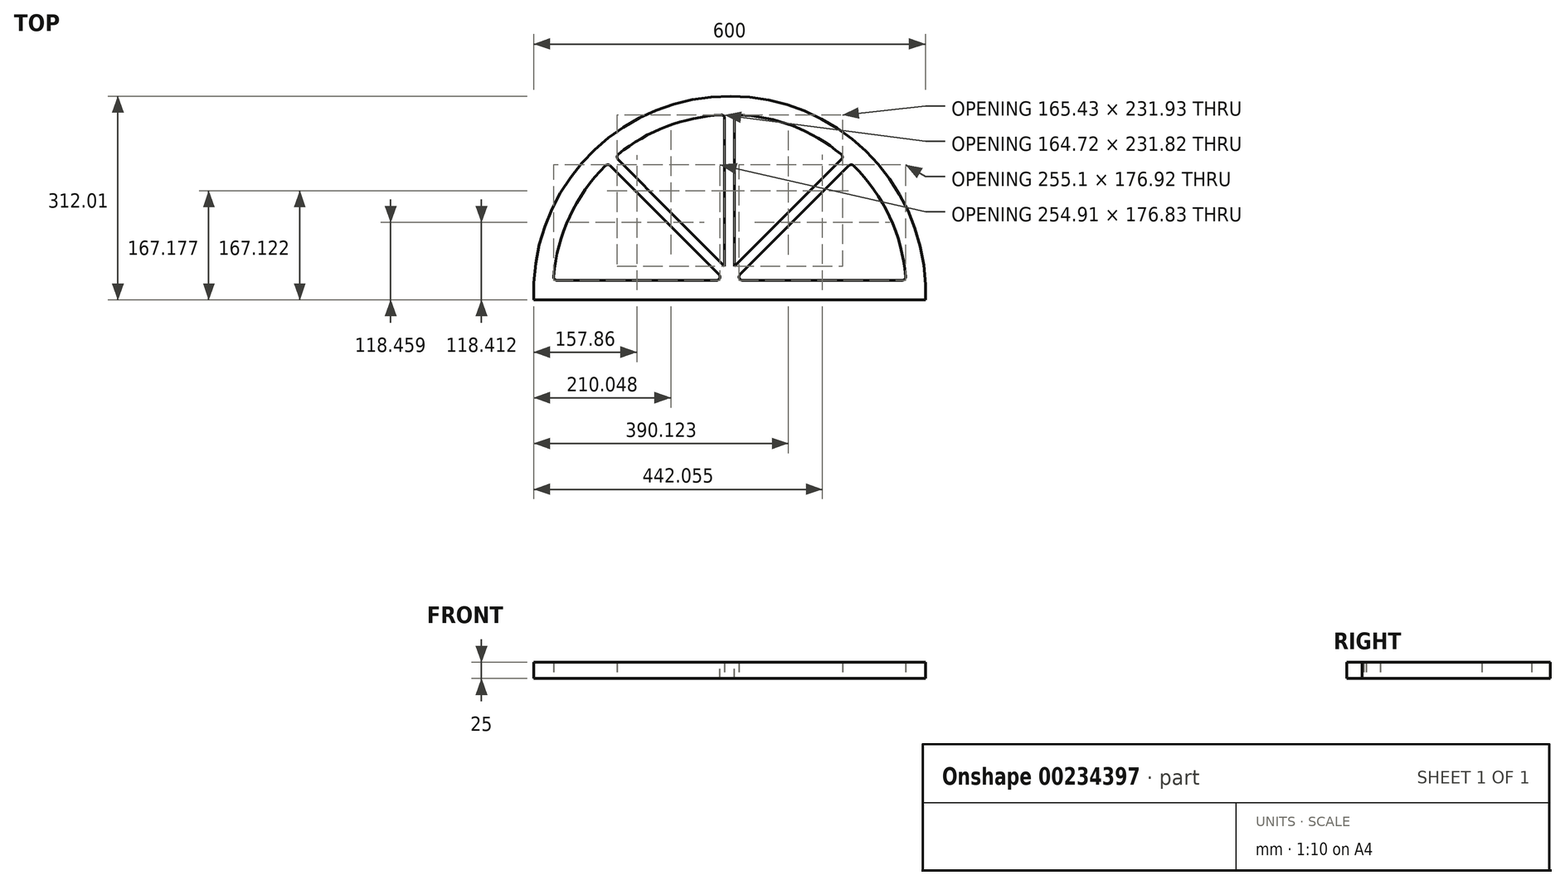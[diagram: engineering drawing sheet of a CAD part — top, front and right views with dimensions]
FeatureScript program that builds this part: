
annotation { "Feature Type Name" : "Feature", "Feature Type Description" : "" }
export const myFeature = defineFeature(function(context is Context, id is Id, definition is map)
    precondition{}
    {
        {
            var Q0;
            Q0=qCreatedBy(makeId("Top.planeOp"),FACE);
            var sketch = newSketch(context, id + "F0", { "sketchPlane" : qUnion([Q0])});
            skLineSegment(sketch, "E0", {"start": v(-299.9, -42.43) * mm, "end": v(300.1, -42.43) * mm});
            skLineSegment(sketch, "E1", {"start": v(-299.9, -42.43) * mm, "end": v(-299.9, -12.43) * mm});
            skLineSegment(sketch, "E2", {"start": v(300.1, -42.43) * mm, "end": v(300.1, -12.43) * mm});
            skArc(sketch, "E3", {"start": v(300.1, -42.43) * mm, "mid": v(-1.39, 269.57) * mm, "end": v(-299.9, -45.27) * mm});
            skLineSegment(sketch, "E4", {"start": v(-299.9, -12.43) * mm, "end": v(-299.7, -12.43) * mm});
            skLineSegment(sketch, "E5", {"start": v(300.1, -12.43) * mm, "end": v(299.77, -12.43) * mm});
            skArc(sketch, "E6", {"start": v(270.1, -12.43) * mm, "mid": v(245.18, 84.94) * mm, "end": v(186.44, 166.5) * mm});
            skPoint(sketch, "E7.start.orphan", {"position": v(0, -42.43) * mm});
            skLineSegment(sketch, "E8", {"start": v(-7.5, 49.69) * mm, "end": v(-7.5, 8.78) * mm});
            skLineSegment(sketch, "E9", {"start": v(-7.5, 49.69) * mm, "end": v(-7.5, 240.8) * mm});
            skLineSegment(sketch, "E10", {"start": v(7.5, 49.69) * mm, "end": v(7.5, 8.78) * mm});
            skPoint(sketch, "E11", {"position": v(-7.5, 240.8) * mm});
            skPoint(sketch, "E12", {"position": v(7.5, 240.8) * mm});
            skLineSegment(sketch, "E13", {"start": v(-269.9, -12.43) * mm, "end": v(-7.5, -12.43) * mm});
            skLineSegment(sketch, "E14", {"start": v(7.5, -12.43) * mm, "end": v(270.1, -12.43) * mm});
            skPoint(sketch, "E15.orphan", {"position": v(-7.5, -42.43) * mm});
            skPoint(sketch, "E16.orphan", {"position": v(7.5, -42.43) * mm});
            skPoint(sketch, "E17", {"position": v(0, -12.47) * mm});
            skLineSegment(sketch, "E18", {"start": v(-7.5, -12.43) * mm, "end": v(-186.35, 166.41) * mm});
            skLineSegment(sketch, "E19", {"start": v(-86.32, 87.6) * mm, "end": v(-174.62, 176.93) * mm});
            skLineSegment(sketch, "E20", {"start": v(-86.32, 87.6) * mm, "end": v(-7.5, 8.78) * mm});
            skPoint(sketch, "E21.start.orphan", {"position": v(-96.92, 76.99) * mm});
            skArc(sketch, "E22.trimOffspring", {"start": v(-186.35, 166.41) * mm, "mid": v(-245.02, 84.88) * mm, "end": v(-269.9, -12.43) * mm});
            skLineSegment(sketch, "E23", {"start": v(7.5, -12.43) * mm, "end": v(186.44, 166.5) * mm});
            skLineSegment(sketch, "E24", {"start": v(86.36, 87.64) * mm, "end": v(7.5, 8.78) * mm});
            skLineSegment(sketch, "E25", {"start": v(86.36, 87.64) * mm, "end": v(175.26, 176.54) * mm});
            skPoint(sketch, "E26.start.orphan", {"position": v(96.97, 77.04) * mm});
            skArc(sketch, "E27.trimOffspring", {"start": v(-7.5, 240.8) * mm, "mid": v(-96.5, 223.08) * mm, "end": v(-174.62, 176.93) * mm});
            skLineSegment(sketch, "E28", {"start": v(7.5, 49.69) * mm, "end": v(7.5, 240.8) * mm});
            skArc(sketch, "E29", {"start": v(175.26, 176.54) * mm, "mid": v(97.2, 223.87) * mm, "end": v(7.5, 240.8) * mm});
            skSolve(sketch);
        }
        {
            var Q0;
            {var subQ2=sQuery(id+"F0.wireOp",EDGE,"E0");Q0=makeQuery(id+"F0.imprint","IMPRINT",FACE,{"disambiguationData":[TD([[makeQuery(id+"F0.imprint","IMPRINT",EDGE,{"derivedFrom":subQ2}),1.0]])]});}
            extrude(context, id + "F1", {"entities" : qUnion([Q0]), "depth" : 25 * mm});
        }
        {
            var Q0;
            Q0=makeQuery(id+"F1.opExtrude","SWEPT_EDGE",EDGE,{"disambiguationData":[OSD([sQuery(id+"F0.wireOp",EDGE,"E9"),sQuery(id+"F0.wireOp",EDGE,"E27.trimOffspring")])]});
            var Q1;
            Q1=makeQuery(id+"F1.opExtrude","SWEPT_EDGE",EDGE,{"disambiguationData":[OSD([sQuery(id+"F0.wireOp",EDGE,"E25"),sQuery(id+"F0.wireOp",EDGE,"E29")])]});
            var Q2;
            Q2=makeQuery(id+"F1.opExtrude","SWEPT_EDGE",EDGE,{"disambiguationData":[OSD([sQuery(id+"F0.wireOp",EDGE,"E6"),sQuery(id+"F0.wireOp",EDGE,"E14")])]});
            var Q3;
            Q3=makeQuery(id+"F1.opExtrude","SWEPT_EDGE",EDGE,{"disambiguationData":[OSD([sQuery(id+"F0.wireOp",EDGE,"E28"),sQuery(id+"F0.wireOp",EDGE,"E29")])]});
            var Q4;
            Q4=makeQuery(id+"F1.opExtrude","SWEPT_EDGE",EDGE,{"disambiguationData":[OSD([sQuery(id+"F0.wireOp",EDGE,"E18"),sQuery(id+"F0.wireOp",EDGE,"E22.trimOffspring")])]});
            var Q5;
            Q5=makeQuery(id+"F1.opExtrude","SWEPT_EDGE",EDGE,{"disambiguationData":[OSD([sQuery(id+"F0.wireOp",EDGE,"E13"),sQuery(id+"F0.wireOp",EDGE,"E22.trimOffspring")])]});
            var Q6;
            Q6=makeQuery(id+"F1.opExtrude","SWEPT_EDGE",EDGE,{"disambiguationData":[OSD([sQuery(id+"F0.wireOp",EDGE,"E6"),sQuery(id+"F0.wireOp",EDGE,"E23")])]});
            var Q7;
            Q7=makeQuery(id+"F1.opExtrude","SWEPT_EDGE",EDGE,{"disambiguationData":[OSD([sQuery(id+"F0.wireOp",EDGE,"E19"),sQuery(id+"F0.wireOp",EDGE,"E27.trimOffspring")])]});
            fillet(context, id + "F2", {"entities" : qUnion([Q0, Q1, Q2, Q3, Q4, Q5, Q6, Q7]), "radius" : 5 * mm, "tangentPropagation" : true, "allowEdgeOverflow" : false});
        }
        {
            var Q0;
            Q0=makeQuery(id+"F1.opExtrude","SWEPT_EDGE",EDGE,{"disambiguationData":[OSD([sQuery(id+"F0.wireOp",EDGE,"E14"),sQuery(id+"F0.wireOp",EDGE,"E23")])]});
            var Q1;
            Q1=makeQuery(id+"F1.opExtrude","SWEPT_EDGE",EDGE,{"disambiguationData":[OSD([sQuery(id+"F0.wireOp",EDGE,"E13"),sQuery(id+"F0.wireOp",EDGE,"E18")])]});
            fillet(context, id + "F3", {"entities" : qUnion([Q0, Q1]), "radius" : 5 * mm, "tangentPropagation" : true, "allowEdgeOverflow" : false});
        }
    });
